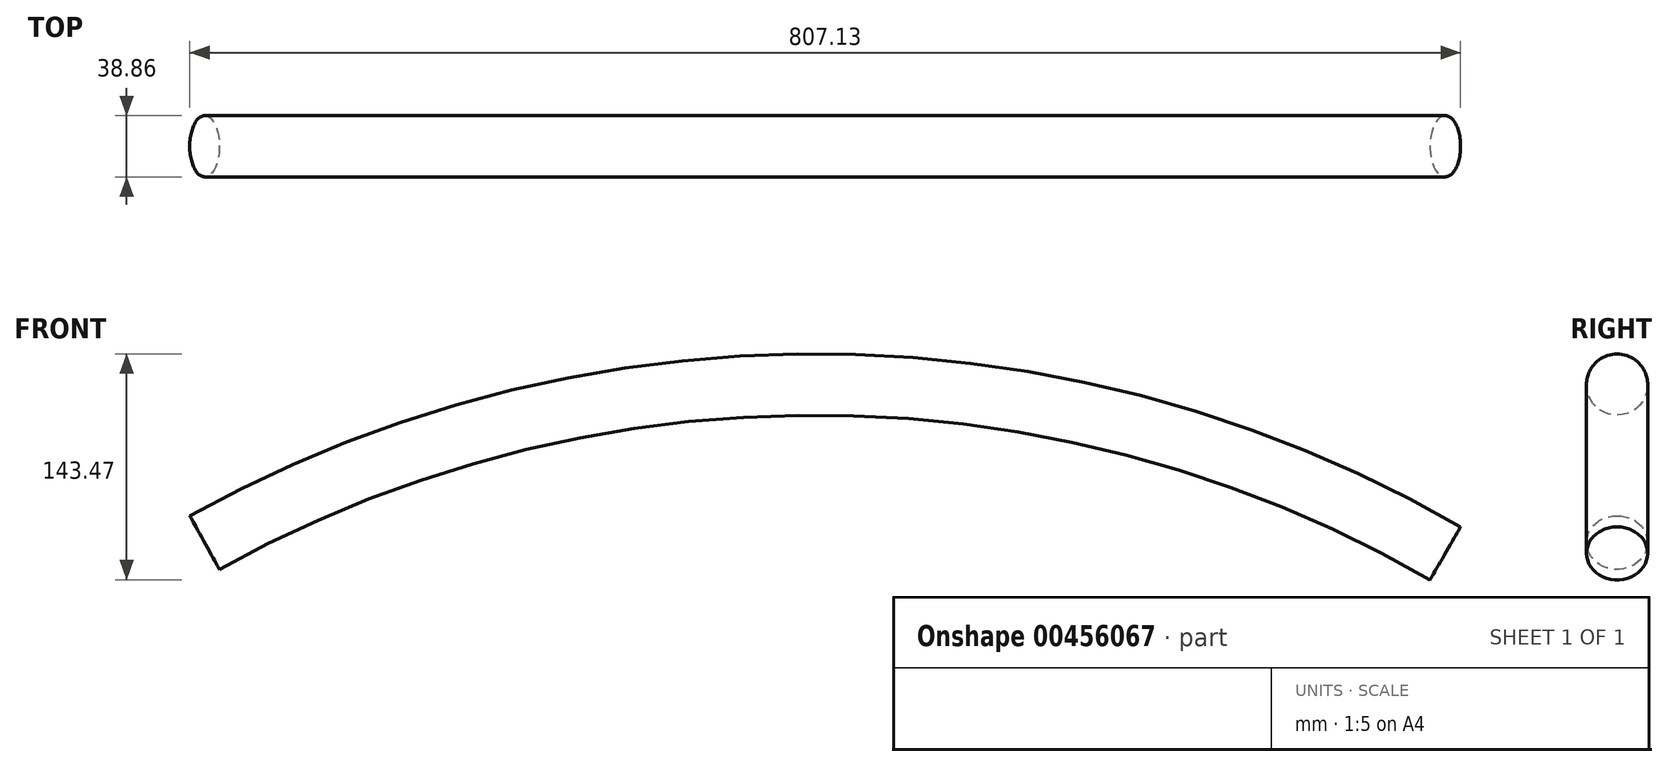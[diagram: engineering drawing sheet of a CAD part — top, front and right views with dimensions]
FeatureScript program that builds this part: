
annotation { "Feature Type Name" : "Feature", "Feature Type Description" : "" }
export const myFeature = defineFeature(function(context is Context, id is Id, definition is map)
    precondition{}
    {
        {
            var Q0;
            Q0=qCreatedBy(makeId("Top.planeOp"),FACE);
            var sketch = newSketch(context, id + "F0", { "sketchPlane" : qUnion([Q0])});
            skLineSegment(sketch, "E0", {"start": v(0, 0) * mm, "end": v(800.15, 0) * mm});
            skCircle(sketch, "E1", {"center": v(800.15, 0) * mm, "radius": 19.43 * mm});
            skLineSegment(sketch, "E2", {"start": v(0, 18.17) * mm, "end": v(0, -26.19) * mm});
            skSolve(sketch);
        }
        {
            var Q0;
            Q0=makeQuery(id+"F0.imprint","IMPRINT",FACE,{"disambiguationData":[TD([[makeQuery(id+"F0.imprint","IMPRINT",EDGE,{"derivedFrom":sQuery(id+"F0.wireOp",EDGE,"E1")}),1.0]])]});
            var Q1;
            Q1=sQuery(id+"F0.wireOp",EDGE,"E2");
            revolve(context, id + "F1", {"entities" : qUnion([Q0]), "axis" : qUnion([Q1]), "revolveType" : RevolveType.TWO_DIRECTIONS, "oppositeDirection" : true, "angle" : 300 * degree, "angleBack" : 241 * degree});
        }
    });
